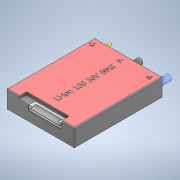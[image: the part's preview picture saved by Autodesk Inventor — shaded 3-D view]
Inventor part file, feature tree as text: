
AUTODESK INVENTOR PART (.ipt)
format: ipt  version: 2020.1 (Build 241239000, 239)  size: 698,880 bytes
history: native  units: mm
features: sketch x3, emboss x2, other x1
ambient origin geometry x8: Origin, YZ Plane, XZ Plane, XY Plane, X Axis, Y Axis, Z Axis, Center Point
bodies: Solid1 (feature_tree)
feature tree (6):
  emboss  "Emboss1"
  sketch  "Sketch2"  dims[d2=0.05mm d3=0.0mm]
  emboss  "Emboss2"
  sketch  "Sketch1"  dims[d0=0.05mm d1=0.0mm]
  sketch  "Sketch3"
  other  "Boss-Extrude6"
